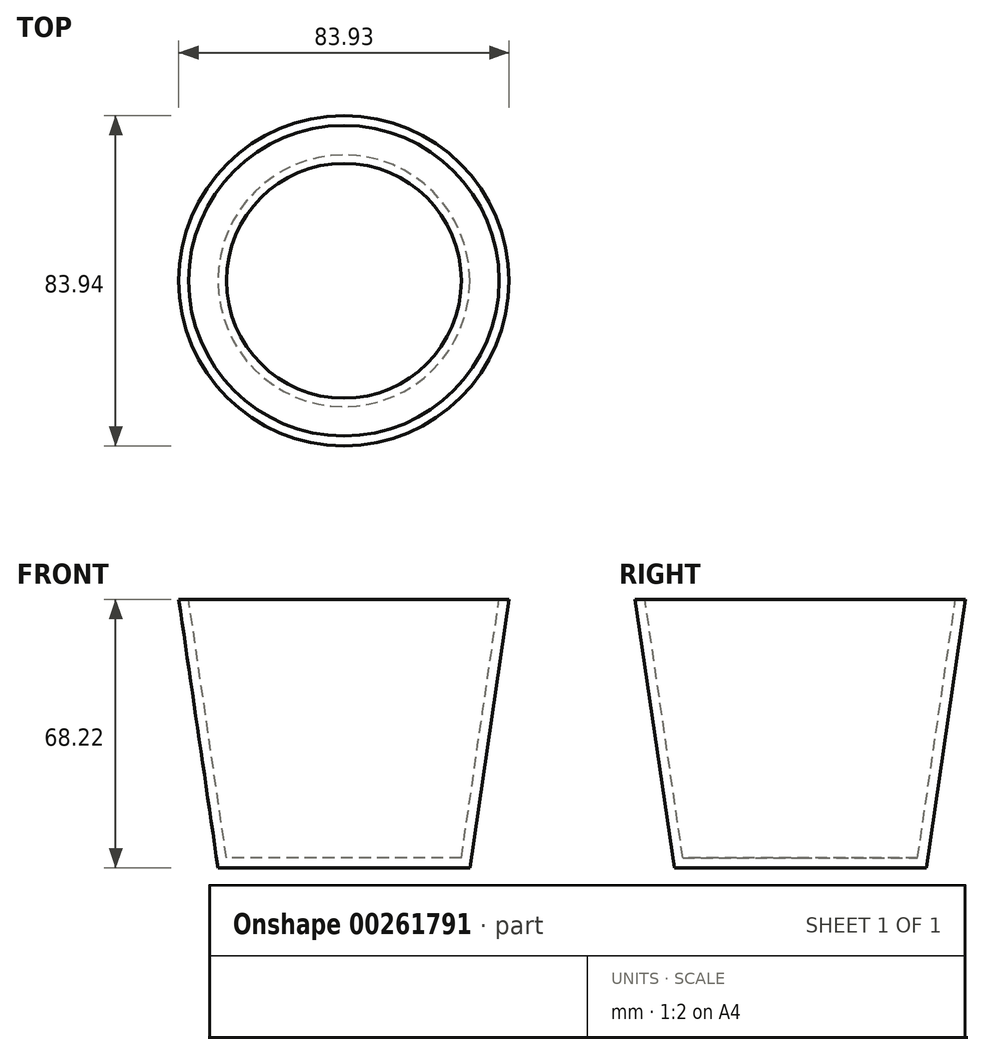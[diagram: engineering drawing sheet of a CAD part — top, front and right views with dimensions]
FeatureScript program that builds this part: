
annotation { "Feature Type Name" : "Feature", "Feature Type Description" : "" }
export const myFeature = defineFeature(function(context is Context, id is Id, definition is map)
    precondition{}
    {
        {
            var Q0;
            Q0=qCreatedBy(makeId("Front.planeOp"),FACE);
            var sketch = newSketch(context, id + "F0", { "sketchPlane" : qUnion([Q0])});
            skLineSegment(sketch, "E0", {"start": v(-206.45, 68.22) * mm, "end": v(-164.48, 68.22) * mm});
            skLineSegment(sketch, "E1", {"start": v(-164.48, 68.22) * mm, "end": v(-174.46, 0) * mm});
            skLineSegment(sketch, "E2", {"start": v(-174.46, 0) * mm, "end": v(-206.45, 0) * mm});
            skLineSegment(sketch, "E3", {"start": v(-206.45, 0) * mm, "end": v(-206.45, 68.22) * mm});
            skSolve(sketch);
        }
        {
            var Q0;
            Q0=makeQuery(id+"F0.imprint","IMPRINT",FACE,{"disambiguationData":[TD([[makeQuery(id+"F0.imprint","IMPRINT",EDGE,{"derivedFrom":sQuery(id+"F0.wireOp",EDGE,"E0")}),-1.0]])]});
            var Q1;
            Q1=sQuery(id+"F0.wireOp",EDGE,"E3");
            revolve(context, id + "F1", {"surfaceOperationType" : NewSurfaceOperationType.NEW, "entities" : qUnion([Q0]), "axis" : qUnion([Q1]), "revolveType" : RevolveType.FULL});
        }
        {
            var Q0;
            Q0=makeQuery(id+"F1.opRevolve","SWEPT_FACE",FACE,{"disambiguationData":[OSD([sQuery(id+"F0.wireOp",EDGE,"E0")])]});
            shell(context, id + "F2", {"entities" : qUnion([Q0]), "thickness" : 2.5 * mm});
        }
    });
